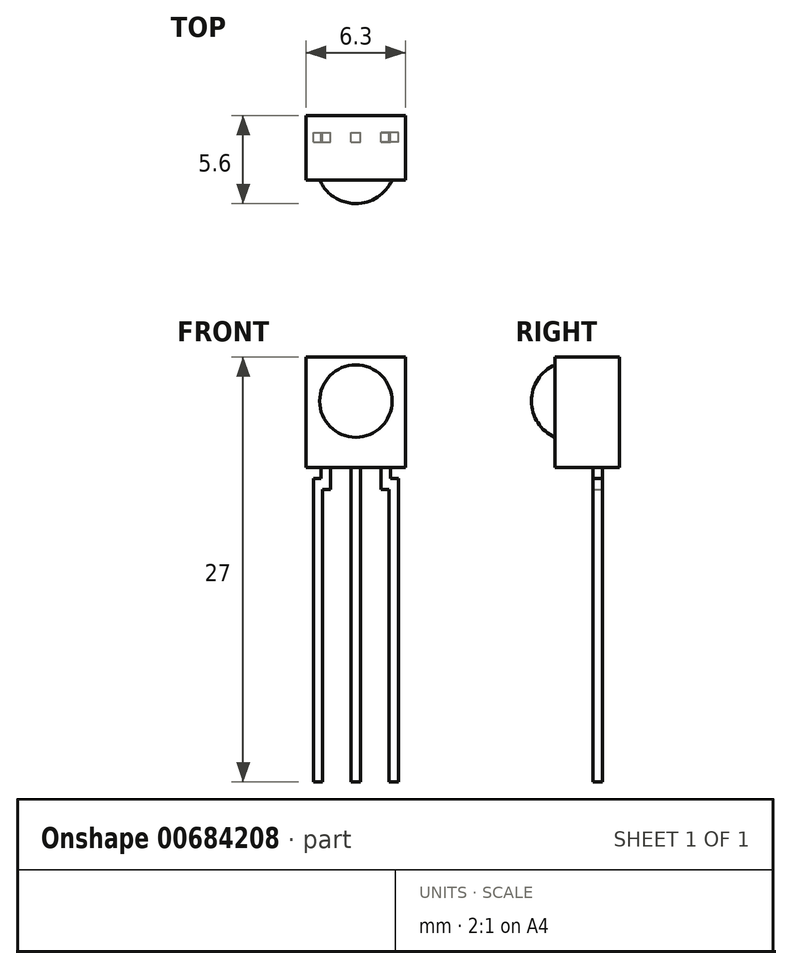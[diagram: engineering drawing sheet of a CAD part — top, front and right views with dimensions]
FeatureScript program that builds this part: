
annotation { "Feature Type Name" : "Feature", "Feature Type Description" : "" }
export const myFeature = defineFeature(function(context is Context, id is Id, definition is map)
    precondition{}
    {
        {
            var Q0;
            Q0=qCreatedBy(makeId("Front.planeOp"),FACE);
            var sketch = newSketch(context, id + "F0", { "sketchPlane" : qUnion([Q0])});
            skLineSegment(sketch, "E0.bottom", {"start": v(-3.15, 2.8) * mm, "end": v(3.15, 2.8) * mm});
            skLineSegment(sketch, "E0.top", {"start": v(-3.15, -4.2) * mm, "end": v(3.15, -4.2) * mm});
            skLineSegment(sketch, "E0.left", {"start": v(-3.15, 2.8) * mm, "end": v(-3.15, -4.2) * mm});
            skLineSegment(sketch, "E0.right", {"start": v(3.15, 2.8) * mm, "end": v(3.15, -4.2) * mm});
            skLineSegment(sketch, "E1.bottom", {"start": v(-0.3, -24.2) * mm, "end": v(0.3, -24.2) * mm});
            skLineSegment(sketch, "E1.top", {"start": v(-0.3, -4.2) * mm, "end": v(0.3, -4.2) * mm});
            skLineSegment(sketch, "E1.left", {"start": v(-0.3, -24.2) * mm, "end": v(-0.3, -4.2) * mm});
            skLineSegment(sketch, "E1.right", {"start": v(0.3, -24.2) * mm, "end": v(0.3, -4.2) * mm});
            skLineSegment(sketch, "E2.bottom", {"start": v(-2.7, -4.9) * mm, "end": v(-2.2, -4.9) * mm});
            skLineSegment(sketch, "E2.top", {"start": v(-2.7, -24.2) * mm, "end": v(-2.1, -24.2) * mm});
            skLineSegment(sketch, "E2.left", {"start": v(-2.7, -4.9) * mm, "end": v(-2.7, -24.2) * mm});
            skLineSegment(sketch, "E2.right", {"start": v(-2.1, -5.6) * mm, "end": v(-2.1, -24.2) * mm});
            skLineSegment(sketch, "E3.bottom", {"start": v(-2.1, -5.6) * mm, "end": v(-1.6, -5.6) * mm});
            skLineSegment(sketch, "E3.top", {"start": v(-2.2, -4.2) * mm, "end": v(-1.6, -4.2) * mm});
            skLineSegment(sketch, "E3.left", {"start": v(-2.2, -4.9) * mm, "end": v(-2.2, -4.2) * mm});
            skLineSegment(sketch, "E3.right", {"start": v(-1.6, -5.6) * mm, "end": v(-1.6, -4.2) * mm});
            skLineSegment(sketch, "E4.MirrorCS", {"start": v(2.7, -24.2) * mm, "end": v(2.1, -24.2) * mm});
            skLineSegment(sketch, "E5.MirrorCS", {"start": v(2.7, -4.9) * mm, "end": v(2.2, -4.9) * mm});
            skLineSegment(sketch, "E6.MirrorCS", {"start": v(2.1, -5.6) * mm, "end": v(1.6, -5.6) * mm});
            skLineSegment(sketch, "E7.MirrorCS", {"start": v(2.2, -4.2) * mm, "end": v(1.6, -4.2) * mm});
            skLineSegment(sketch, "E8.MirrorCS", {"start": v(2.2, -4.9) * mm, "end": v(2.2, -4.2) * mm});
            skLineSegment(sketch, "E9.MirrorCS", {"start": v(2.7, -4.9) * mm, "end": v(2.7, -24.2) * mm});
            skLineSegment(sketch, "E10.MirrorCS", {"start": v(2.1, -5.6) * mm, "end": v(2.1, -24.2) * mm});
            skLineSegment(sketch, "E11.MirrorCS", {"start": v(1.6, -5.6) * mm, "end": v(1.6, -4.2) * mm});
            skSolve(sketch);
        }
        {
            var Q0;
            Q0=makeQuery(id+"F0.imprint","IMPRINT",FACE,{"disambiguationData":[TD([[makeQuery(id+"F0.imprint","IMPRINT",EDGE,{"derivedFrom":sQuery(id+"F0.wireOp",EDGE,"E0.bottom")}),-1.0]])]});
            extrude(context, id + "F1", {"entities" : qUnion([Q0]), "depth" : 2.7 * mm, "offsetDistance" : 25 * mm, "hasSecondDirection" : true, "secondDirectionOppositeDirection" : true, "secondDirectionDepth" : 1.4 * mm});
        }
        {
            var Q0;
            Q0=makeQuery(id+"F0.imprint","IMPRINT",FACE,{"disambiguationData":[TD([[makeQuery(id+"F0.imprint","IMPRINT",EDGE,{"derivedFrom":sQuery(id+"F0.wireOp",EDGE,"E2.bottom")}),-1.0]])]});
            var Q1;
            Q1=makeQuery(id+"F0.imprint","IMPRINT",FACE,{"disambiguationData":[TD([[makeQuery(id+"F0.imprint","IMPRINT",EDGE,{"derivedFrom":sQuery(id+"F0.wireOp",EDGE,"E1.bottom")}),1.0]])]});
            var Q2;
            Q2=makeQuery(id+"F0.imprint","IMPRINT",FACE,{"disambiguationData":[TD([[makeQuery(id+"F0.imprint","IMPRINT",EDGE,{"derivedFrom":sQuery(id+"F0.wireOp",EDGE,"E4.MirrorCS")}),-1.0]])]});
            extrude(context, id + "F2", {"entities" : qUnion([Q0, Q1, Q2]), "operationType" : NewBodyOperationType.ADD, "depth" : 0.6 * mm, "offsetDistance" : 25 * mm, "symmetric" : true});
        }
        {
            var Q0;
            Q0=qCreatedBy(makeId("Top.planeOp"),FACE);
            var sketch = newSketch(context, id + "F3", { "sketchPlane" : qUnion([Q0])});
            skArc(sketch, "E12", {"start": v(2.3, -2.7) * mm, "mid": v(0, -4.2) * mm, "end": v(-2.3, -2.7) * mm});
            skLineSegment(sketch, "E13", {"start": v(0, 0) * mm, "end": v(0, -8) * mm, "construction": true});
            skLineSegment(sketch, "E14", {"start": v(2.3, -2.7) * mm, "end": v(0, -2.7) * mm});
            skLineSegment(sketch, "E15", {"start": v(0, -2.7) * mm, "end": v(0, -4.2) * mm});
            skSolve(sketch);
        }
        {
            var Q0;
            Q0 = qSketchRegion(id + "F3", true);
            var Q1;
            Q1=sQuery(id+"F3.wireOp",EDGE,"E13");
            revolve(context, id + "F4", {"operationType" : NewBodyOperationType.ADD, "surfaceOperationType" : NewSurfaceOperationType.NEW, "entities" : qUnion([Q0]), "axis" : qUnion([Q1]), "revolveType" : RevolveType.FULL});
        }
    });
